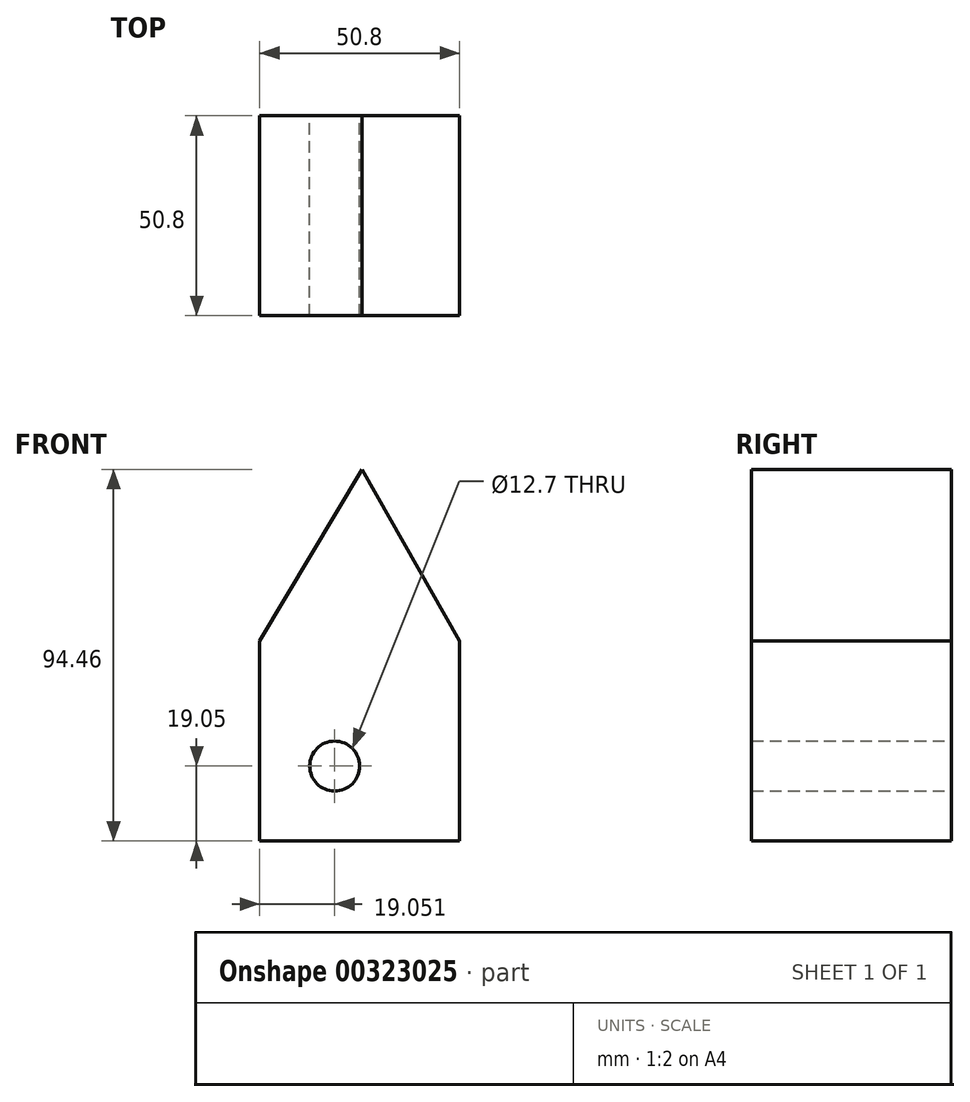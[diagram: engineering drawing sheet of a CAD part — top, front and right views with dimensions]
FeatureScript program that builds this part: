
annotation { "Feature Type Name" : "Feature", "Feature Type Description" : "" }
export const myFeature = defineFeature(function(context is Context, id is Id, definition is map)
    precondition{}
    {
        {
            var Q0;
            Q0=qCreatedBy(makeId("Front.planeOp"),FACE);
            var sketch = newSketch(context, id + "F0", { "sketchPlane" : qUnion([Q0])});
            skLineSegment(sketch, "E0.top", {"start": v(-25.97, -25.92) * mm, "end": v(24.83, -25.92) * mm});
            skLineSegment(sketch, "E0.left", {"start": v(-25.97, 24.88) * mm, "end": v(-25.97, -25.92) * mm});
            skLineSegment(sketch, "E1", {"start": v(24.83, 24.88) * mm, "end": v(0, 68.54) * mm});
            skLineSegment(sketch, "E2", {"start": v(-25.97, 24.88) * mm, "end": v(0, 68.54) * mm});
            skLineSegment(sketch, "E3", {"start": v(24.83, 24.88) * mm, "end": v(24.83, -25.92) * mm});
            skCircle(sketch, "E4", {"center": v(-6.92, -6.87) * mm, "radius": 6.35 * mm});
            skSolve(sketch);
        }
        {
            var Q0;
            Q0=makeQuery(id+"F0.imprint","IMPRINT",FACE,{"disambiguationData":[TD([[makeQuery(id+"F0.imprint","IMPRINT",EDGE,{"derivedFrom":sQuery(id+"F0.wireOp",EDGE,"E0.top")}),1.0]])]});
            extrude(context, id + "F1", {"entities" : qUnion([Q0]), "depth" : 50.8 * mm});
        }
    });
